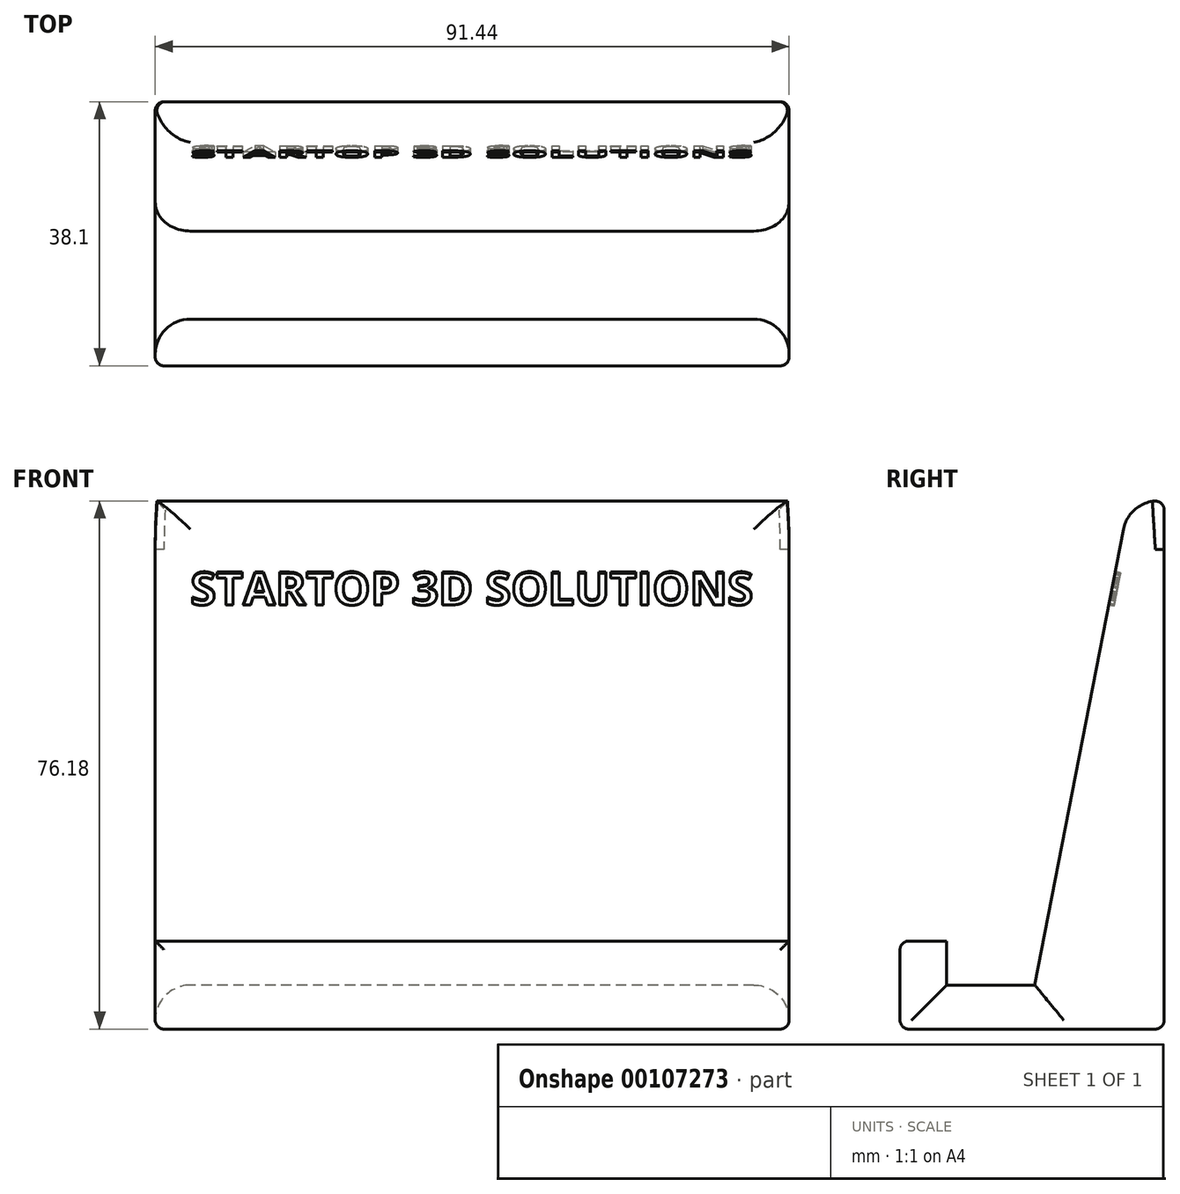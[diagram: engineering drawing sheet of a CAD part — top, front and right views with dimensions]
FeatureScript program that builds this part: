
annotation { "Feature Type Name" : "Feature", "Feature Type Description" : "" }
export const myFeature = defineFeature(function(context is Context, id is Id, definition is map)
    precondition{}
    {
        {
            var Q0;
            Q0=qCreatedBy(makeId("Right.planeOp"),FACE);
            var sketch = newSketch(context, id + "F0", { "sketchPlane" : qUnion([Q0])});
            skLineSegment(sketch, "E0", {"start": v(0, 0) * mm, "end": v(38.1, 0) * mm});
            skLineSegment(sketch, "E1", {"start": v(38.1, 0) * mm, "end": v(38.1, 76.2) * mm});
            skLineSegment(sketch, "E2", {"start": v(38.1, 76.2) * mm, "end": v(33.02, 76.2) * mm});
            skLineSegment(sketch, "E3", {"start": v(33.02, 76.2) * mm, "end": v(19.44, 6.35) * mm});
            skLineSegment(sketch, "E4", {"start": v(19.44, 6.35) * mm, "end": v(6.74, 6.35) * mm});
            skLineSegment(sketch, "E5", {"start": v(6.74, 6.35) * mm, "end": v(6.74, 12.7) * mm});
            skLineSegment(sketch, "E6", {"start": v(6.74, 12.7) * mm, "end": v(0, 12.7) * mm});
            skLineSegment(sketch, "E7", {"start": v(0, 12.7) * mm, "end": v(0, 0) * mm});
            skSolve(sketch);
        }
        {
            var Q0;
            Q0=makeQuery(id+"F0.imprint","IMPRINT",FACE,{"disambiguationData":[TD([[makeQuery(id+"F0.imprint","IMPRINT",EDGE,{"derivedFrom":sQuery(id+"F0.wireOp",EDGE,"E0")}),1.0]])]});
            extrude(context, id + "F1", {"entities" : qUnion([Q0]), "depth" : 91.44 * mm});
        }
        {
            var Q0;
            Q0=makeQuery(id+"F1.opExtrude","SWEPT_EDGE",EDGE,{"disambiguationData":[OSD([sQuery(id+"F0.wireOp",EDGE,"E2"),sQuery(id+"F0.wireOp",EDGE,"E3")])]});
            var Q1;
            Q1=makeQuery(id+"F1.opExtrude","CAP_EDGE",EDGE,{"disambiguationData":[OSD([sQuery(id+"F0.wireOp",EDGE,"E3")])],"isStart":false});
            var Q2;
            Q2=makeQuery(id+"F1.opExtrude","CAP_EDGE",EDGE,{"disambiguationData":[OSD([sQuery(id+"F0.wireOp",EDGE,"E3")])],"isStart":true});
            var Q3;
            Q3=makeQuery(id+"F1.opExtrude","CAP_EDGE",EDGE,{"disambiguationData":[OSD([sQuery(id+"F0.wireOp",EDGE,"E4")])],"isStart":false});
            var Q4;
            Q4=makeQuery(id+"F1.opExtrude","CAP_EDGE",EDGE,{"disambiguationData":[OSD([sQuery(id+"F0.wireOp",EDGE,"E4")])],"isStart":true});
            var Q5;
            Q5=makeQuery(id+"F1.opExtrude","CAP_EDGE",EDGE,{"disambiguationData":[OSD([sQuery(id+"F0.wireOp",EDGE,"E5")])],"isStart":true});
            var Q6;
            Q6=makeQuery(id+"F1.opExtrude","CAP_EDGE",EDGE,{"disambiguationData":[OSD([sQuery(id+"F0.wireOp",EDGE,"E5")])],"isStart":false});
            fillet(context, id + "F2", {"entities" : qUnion([Q0, Q1, Q2, Q3, Q4, Q5, Q6]), "radius" : 5.08 * mm, "tangentPropagation" : true, "allowEdgeOverflow" : false});
        }
        {
            var Q0;
            Q0=makeQuery(id+"F1.opExtrude","CAP_EDGE",EDGE,{"disambiguationData":[OSD([sQuery(id+"F0.wireOp",EDGE,"E1")])],"isStart":true});
            var Q1;
            Q1=makeQuery(id+"F1.opExtrude","SWEPT_EDGE",EDGE,{"disambiguationData":[OSD([sQuery(id+"F0.wireOp",EDGE,"E0"),sQuery(id+"F0.wireOp",EDGE,"E1")])]});
            var Q2;
            Q2=makeQuery(id+"F1.opExtrude","CAP_EDGE",EDGE,{"disambiguationData":[OSD([sQuery(id+"F0.wireOp",EDGE,"E0")])],"isStart":true});
            var Q3;
            Q3=makeQuery(id+"F1.opExtrude","CAP_EDGE",EDGE,{"disambiguationData":[OSD([sQuery(id+"F0.wireOp",EDGE,"E1")])],"isStart":false});
            var Q4;
            Q4=makeQuery(id+"F1.opExtrude","CAP_EDGE",EDGE,{"disambiguationData":[OSD([sQuery(id+"F0.wireOp",EDGE,"E0")])],"isStart":false});
            var Q5;
            Q5=makeQuery(id+"F1.opExtrude","CAP_EDGE",EDGE,{"disambiguationData":[OSD([sQuery(id+"F0.wireOp",EDGE,"E7")])],"isStart":false});
            var Q6;
            Q6=makeQuery(id+"F1.opExtrude","SWEPT_EDGE",EDGE,{"disambiguationData":[OSD([sQuery(id+"F0.wireOp",EDGE,"E6"),sQuery(id+"F0.wireOp",EDGE,"E7")])]});
            var Q7;
            Q7=makeQuery(id+"F1.opExtrude","SWEPT_EDGE",EDGE,{"disambiguationData":[OSD([sQuery(id+"F0.wireOp",EDGE,"E0"),sQuery(id+"F0.wireOp",EDGE,"E7")])]});
            var Q8;
            Q8=makeQuery(id+"F1.opExtrude","CAP_EDGE",EDGE,{"disambiguationData":[OSD([sQuery(id+"F0.wireOp",EDGE,"E7")])],"isStart":true});
            var Q9;
            Q9=makeQuery(id+"F1.opExtrude","SWEPT_EDGE",EDGE,{"disambiguationData":[OSD([sQuery(id+"F0.wireOp",EDGE,"E1"),sQuery(id+"F0.wireOp",EDGE,"E2")])]});
            fillet(context, id + "F3", {"entities" : qUnion([Q0, Q1, Q2, Q3, Q4, Q5, Q6, Q7, Q8, Q9]), "radius" : 1.27 * mm, "tangentPropagation" : true, "allowEdgeOverflow" : false});
        }
        {
            var Q0;
            Q0=makeQuery(id+"F1.opExtrude","SWEPT_FACE",FACE,{"disambiguationData":[OSD([sQuery(id+"F0.wireOp",EDGE,"E3")])]});
            var sketch = newSketch(context, id + "F4", { "sketchPlane" : qUnion([Q0])});
            skText(sketch, "E8", { "text": "STARTOP 3D SOLUTIONS", "fontName": "OpenSans-Bold.ttf"});
            const initialGuessF4  = {"E8": [0.00508, 0.06582, 1, 0, 0.00485]};
            skSetInitialGuess(sketch, initialGuessF4);
            skSolve(sketch);
        }
        {
            var Q0;
            Q0 = qSketchRegion(id + "F4", true);
            extrude(context, id + "F5", {"entities" : qUnion([Q0]), "operationType" : NewBodyOperationType.REMOVE, "oppositeDirection" : true, "depth" : 0.76 * mm});
        }
    });
